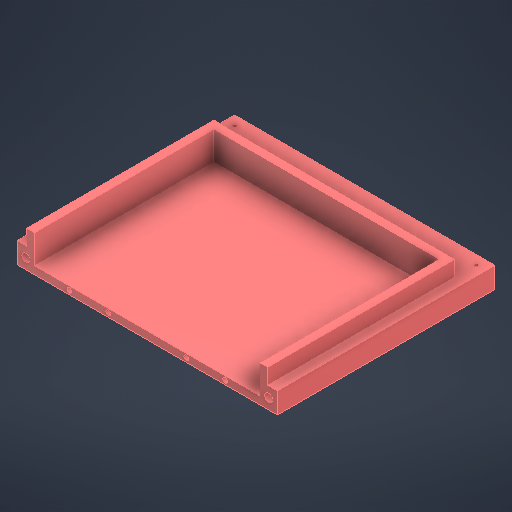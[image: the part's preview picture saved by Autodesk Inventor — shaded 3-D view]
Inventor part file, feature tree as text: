
AUTODESK INVENTOR PART (.ipt)
format: ipt  version: 2025.2 (Build 292293000, 293)  size: 325,120 bytes
history: native  units: in
note: dims shown in document units (in); Inventor stores cm internally (conversion verified against a paired STEP export)
features: sketch x10, extrude x7, split x3, plane x1
ambient origin geometry x8: Origin, YZ Plane, XZ Plane, XY Plane, X Axis, Y Axis, Z Axis, Center Point
bodies: Solid1 (feature_tree)
feature tree (21):
  extrude  "Extrusion1"  Depth=6.5748in
  extrude  "Extrusion2"  Depth=5.689in
  extrude  "Extrusion4"  Depth=0.3307in TaperAngle=0.0deg
  extrude  "Extrusion5"  Depth=0.0984in
  extrude  "Extrusion6"  Depth=0.0984in
  sketch  "Sketch8"  dims[d20=0.2362in d21=0.2362in]
  sketch  "Sketch9"  dims[d22=0.0984in d23=0.2362in]
  split  "Split1"
  split  "Split2"
  split  "Split3"
  plane  "Work Plane1"
  extrude  "Extrusion7"  Depth=0.2362in
  extrude  "Extrusion8"  Depth=0.0984in
  sketch  "Sketch1"  dims[d0=6.5748in d1=10.9843in]
  sketch  "Sketch2"  dims[d2=0.5276in d3=0.0in d4=5.689in]
  sketch  "Sketch4"  dims[d5=9.0591in d6=0.3307in d7=0.0in]
  sketch  "Sketch5"  dims[d16=0.0984in d17=0.2362in]
  sketch  "Sketch7"  dims[d18=0.2362in d19=0.0984in]
  sketch  "Sketch10"  dims[d24=0.2362in]
  sketch  "Sketch11"  dims[d25=0.0984in]
  sketch  "Sketch12"  dims[d26=0.2362in d27=0.2362in d28=0.3937in d29=0.0in d30=0.1969in d31=0.1969in d32=9.4528in d33=0.1969in d34=0.1969in d35=9.4528in d36=0.3937in d37=0.0in d42=0.1378in d43=0.1378in d44=0.1378in d45=0.1378in d46=0.4488in d47=0.0in d48=6.5812in d49=0.0in d51=0.1969in d53=0.1969in d55=0.1181in d57=0.1181in d59=0.1181in d61=0.1181in d62=0.5906in d63=0.0in d50=0.0197in]
